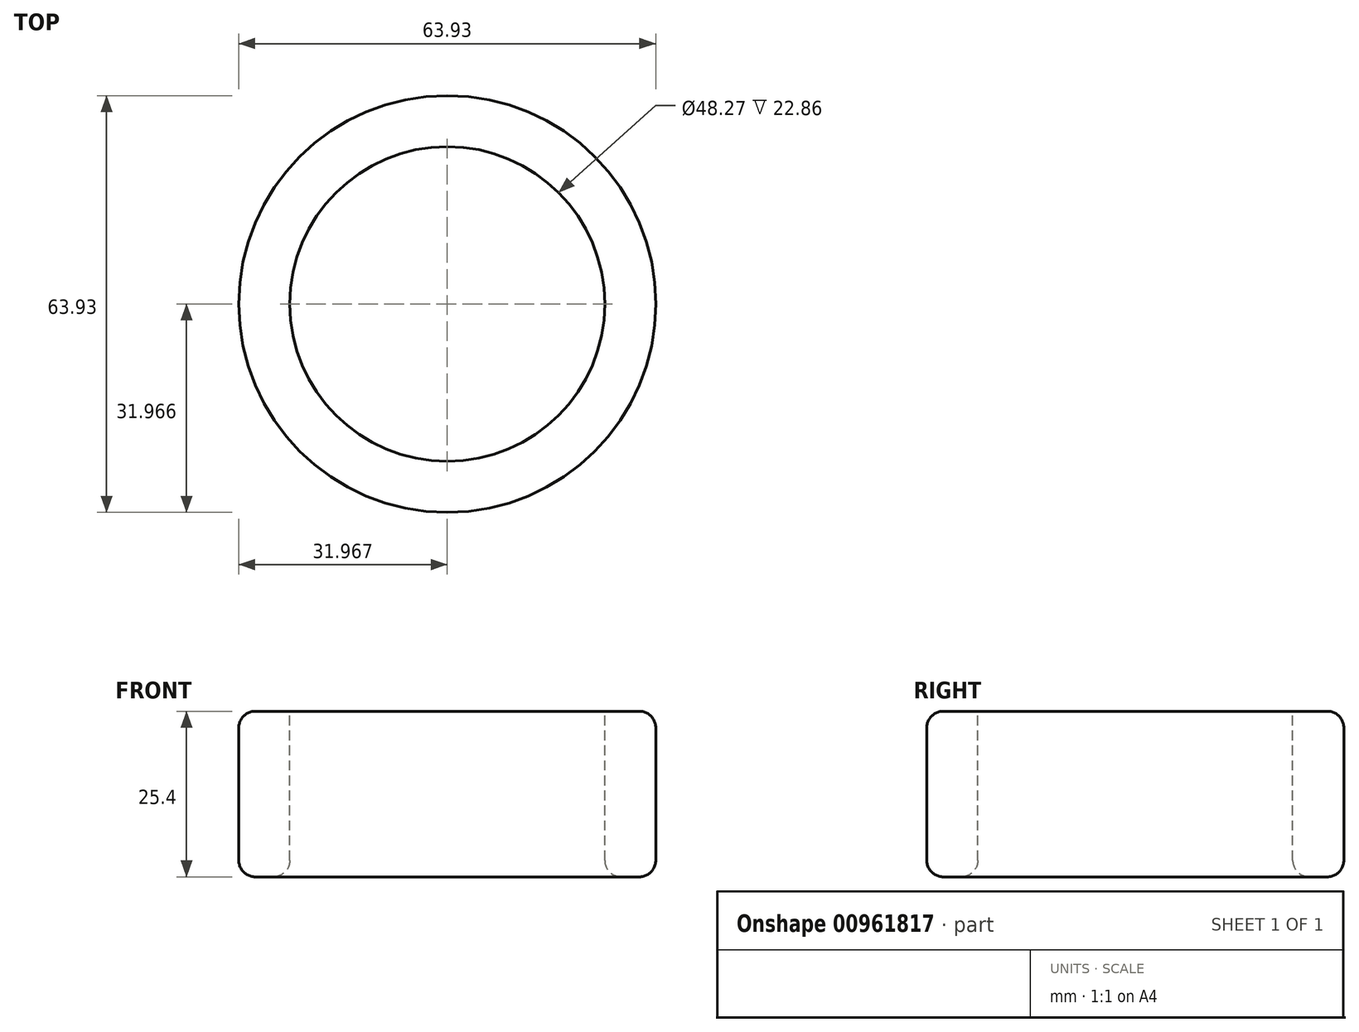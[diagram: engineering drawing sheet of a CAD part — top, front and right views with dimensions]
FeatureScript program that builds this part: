
annotation { "Feature Type Name" : "Feature", "Feature Type Description" : "" }
export const myFeature = defineFeature(function(context is Context, id is Id, definition is map)
    precondition{}
    {
        {
            var Q0;
            Q0=qCreatedBy(makeId("Top.planeOp"),FACE);
            var sketch = newSketch(context, id + "F0", { "sketchPlane" : qUnion([Q0])});
            skCircle(sketch, "E0", {"center": v(-24.4, 20.66) * mm, "radius": 31.96 * mm});
            skSolve(sketch);
        }
        {
            var Q0;
            Q0=makeQuery(id+"F0.imprint","IMPRINT",FACE,{"disambiguationData":[TD([[makeQuery(id+"F0.imprint","IMPRINT",EDGE,{"derivedFrom":sQuery(id+"F0.wireOp",EDGE,"E0")}),1.0]])]});
            extrude(context, id + "F1", {"entities" : qUnion([Q0]), "depth" : 25.4 * mm, "offsetDistance" : 25.4 * mm});
        }
        {
            var Q0;
            Q0=makeQuery(id+"F1.opExtrude","CAP_FACE",FACE,{"disambiguationData":[OSD([sQuery(id+"F0.wireOp",EDGE,"E0")])],"isStart":false});
            var sketch = newSketch(context, id + "F2", { "sketchPlane" : qUnion([Q0])});
            skCircle(sketch, "E1", {"center": v(-24.4, 20.66) * mm, "radius": 24.14 * mm});
            skSolve(sketch);
        }
        {
            var Q0;
            Q0 = qSketchRegion(id + "F2", true);
            extrude(context, id + "F3", {"entities" : qUnion([Q0]), "operationType" : NewBodyOperationType.REMOVE, "endBound" : BoundingType.THROUGH_ALL, "oppositeDirection" : true, "depth" : 25.4 * mm, "offsetDistance" : 25.4 * mm});
        }
        {
            var Q0;
            Q0=makeQuery(id+"F1.opExtrude","CAP_EDGE",EDGE,{"disambiguationData":[OSD([sQuery(id+"F0.wireOp",EDGE,"E0")])],"isStart":false});
            var Q1;
            Q1=makeQuery(id+"F1.opExtrude","CAP_EDGE",EDGE,{"disambiguationData":[OSD([sQuery(id+"F0.wireOp",EDGE,"E0")])],"isStart":true});
            var Q2;
            Q2=makeQuery(id+"F1.opExtrude","SWEPT_FACE",FACE,{"disambiguationData":[OSD([sQuery(id+"F0.wireOp",EDGE,"E0")])]});
            var Q3;
            Q3=makeQuery(id+"F3.boolean.opBoolean","COPY",EDGE,{"derivedFrom":makeQuery(id+"F3.opExtrude","CAP_EDGE",EDGE,{"disambiguationData":[OSD([sQuery(id+"F2.wireOp",EDGE,"E1")])],"isStart":true})});
            var Q4;
            Q4=makeQuery(id+"F3.boolean.opBoolean","INTERSECT",EDGE,{"derivedFrom":[makeQuery(id+"F1.opExtrude","CAP_FACE",FACE,{"disambiguationData":[OSD([sQuery(id+"F0.wireOp",EDGE,"E0")])],"isStart":true}),makeQuery(id+"F3.opExtrude","SWEPT_FACE",FACE,{"disambiguationData":[OSD([sQuery(id+"F2.wireOp",EDGE,"E1")])]})]});
            fillet(context, id + "F4", {"entities" : qUnion([Q0, Q1, Q2, Q3, Q4]), "radius" : 2.54 * mm, "tangentPropagation" : true, "allowEdgeOverflow" : false});
        }
    });
